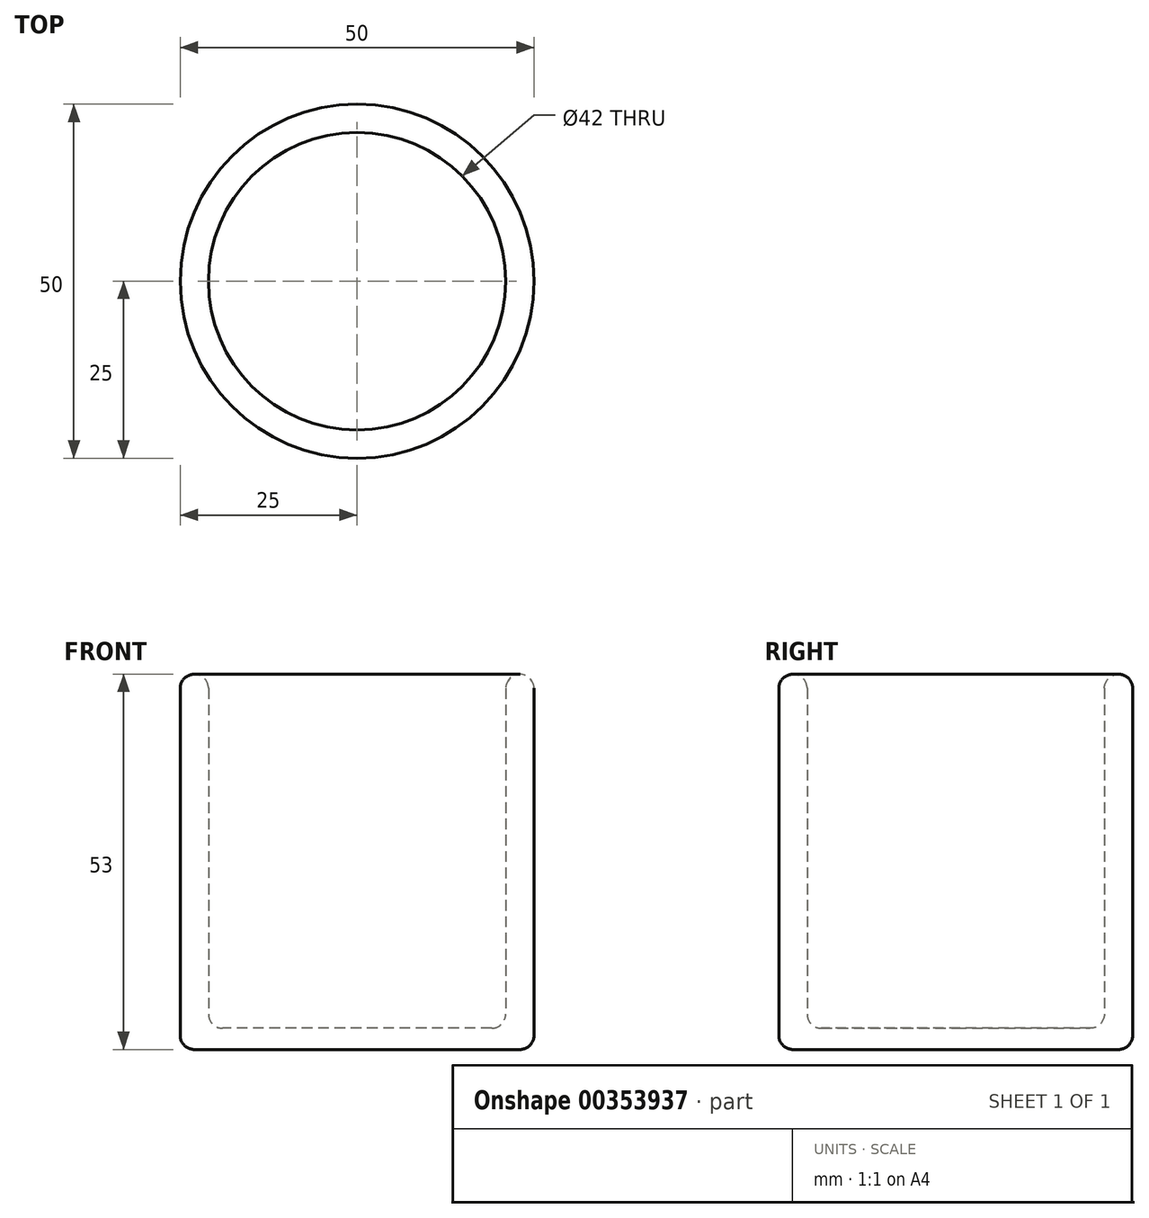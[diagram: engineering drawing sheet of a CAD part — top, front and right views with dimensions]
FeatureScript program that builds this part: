
annotation { "Feature Type Name" : "Feature", "Feature Type Description" : "" }
export const myFeature = defineFeature(function(context is Context, id is Id, definition is map)
    precondition{}
    {
        {
            var Q0;
            Q0=qCreatedBy(makeId("Top.planeOp"),FACE);
            var sketch = newSketch(context, id + "F0", { "sketchPlane" : qUnion([Q0])});
            skCircle(sketch, "E0", {"center": v(0, 0) * mm, "radius": 25 * mm});
            skSolve(sketch);
        }
        {
            var Q0;
            Q0=qSketchRegion(id+"F0",true);
            extrude(context, id + "F1", {"entities" : qUnion([Q0]), "depth" : 3 * mm});
        }
        {
            var Q0;
            Q0=makeQuery(id+"F1.opExtrude","CAP_FACE",FACE,{"disambiguationData":[OSD([sQuery(id+"F0.wireOp",EDGE,"E0")])],"isStart":false});
            var sketch = newSketch(context, id + "F2", { "sketchPlane" : qUnion([Q0])});
            skCircle(sketch, "E1", {"center": v(0, 0) * mm, "radius": 21 * mm});
            skSolve(sketch);
        }
        {
            var Q0;
            Q0=makeQuery(id+"F2.imprint","IMPRINT",FACE,{"disambiguationData":[TD([[makeQuery(id+"F2.imprint","IMPRINT",EDGE,{"derivedFrom":sQuery(id+"F2.wireOp",EDGE,"E1")}),-1.0]])]});
            extrude(context, id + "F3", {"entities" : qUnion([Q0]), "operationType" : NewBodyOperationType.ADD, "depth" : 50 * mm});
        }
        {
            var Q0;
            Q0=makeQuery(id+"F3.opExtrude","CAP_EDGE",EDGE,{"disambiguationData":[OSD([sQuery(id+"F0.wireOp",EDGE,"E0")])],"isStart":false});
            var Q1;
            Q1=makeQuery(id+"F3.opExtrude","CAP_EDGE",EDGE,{"disambiguationData":[OSD([sQuery(id+"F2.wireOp",EDGE,"E1")])],"isStart":false});
            var Q2;
            Q2=makeQuery(id+"F3.opExtrude","CAP_EDGE",EDGE,{"disambiguationData":[OSD([sQuery(id+"F2.wireOp",EDGE,"E1")])],"isStart":true});
            var Q3;
            Q3=makeQuery(id+"F1.opExtrude","CAP_FACE",FACE,{"disambiguationData":[OSD([sQuery(id+"F0.wireOp",EDGE,"E0")])],"isStart":false});
            fillet(context, id + "F4", {"entities" : qUnion([Q0, Q1, Q2, Q3]), "radius" : 2 * mm, "tangentPropagation" : true, "allowEdgeOverflow" : false});
        }
        {
            var Q0;
            Q0=makeQuery(id+"F1.opExtrude","CAP_EDGE",EDGE,{"disambiguationData":[OSD([sQuery(id+"F0.wireOp",EDGE,"E0")])],"isStart":true});
            fillet(context, id + "F5", {"entities" : qUnion([Q0]), "radius" : 2 * mm, "tangentPropagation" : true, "allowEdgeOverflow" : false});
        }
    });
